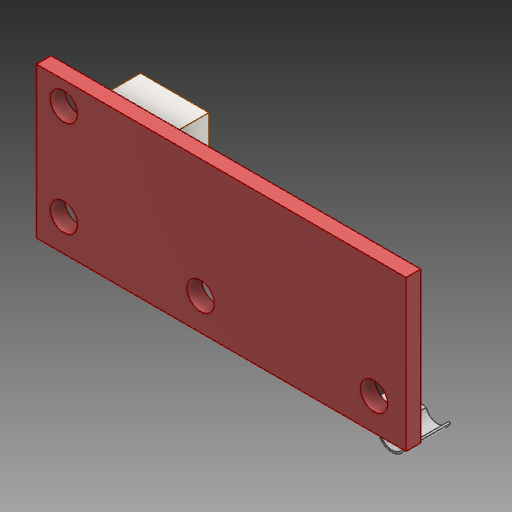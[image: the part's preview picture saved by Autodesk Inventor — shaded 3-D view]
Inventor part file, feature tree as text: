
AUTODESK INVENTOR PART (.ipt)
format: ipt  version: 2017 (Build 210142000, 142)  size: 123,904 bytes
history: mixed  units: mm
features: other x3, extrude x1, imported_body x1
ambient origin geometry x8: Origin, YZ Plane, XZ Plane, XY Plane, X Axis, Y Axis, Z Axis, Center Point
bodies: Solid1 (imported_parasolid), Solid2 (imported_parasolid), Solid3 (imported_parasolid), Solid4 (imported_parasolid)
feature tree (5):
  other  "Boss-Extrude1"
  other  "Boss-Extrude2"
  other  "Cut-Extrude1"
  extrude  "Extrude-Thin1"  [1 undecoded]
  imported_body  NMx_Import_Brep_tag  [imported B-rep: ~38 faces, bbox_mm=[40.5, 7.6, 19.003843]]
note: 1 required parameter value undecoded (feature->parameter linkage not recoverable at this tier; creation-order binding heuristic only, values carry confidence <= 0.55)
